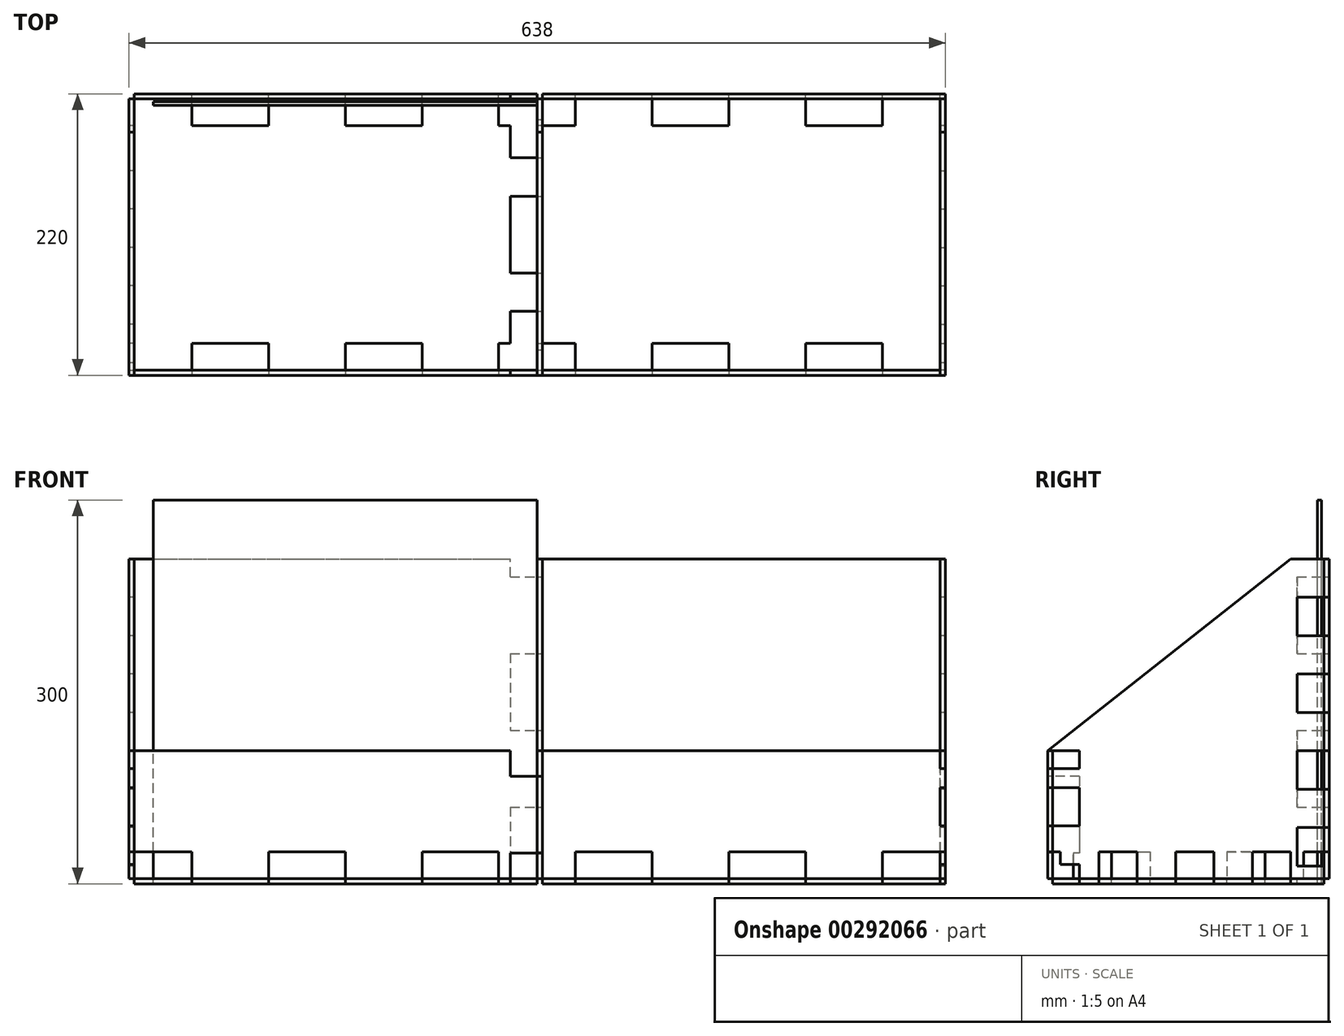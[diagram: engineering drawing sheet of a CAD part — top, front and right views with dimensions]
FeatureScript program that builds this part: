
annotation { "Feature Type Name" : "Feature", "Feature Type Description" : "" }
export const myFeature = defineFeature(function(context is Context, id is Id, definition is map)
    precondition{}
    {
        {
            var Q0;
            Q0=qCreatedBy(makeId("Top.planeOp"),FACE);
            var sketch = newSketch(context, id + "F0", { "sketchPlane" : qUnion([Q0])});
            skLineSegment(sketch, "E0.bottom", {"start": v(-319, 110) * mm, "end": v(319, 110) * mm});
            skLineSegment(sketch, "E0.top", {"start": v(-319, -110) * mm, "end": v(319, -110) * mm});
            skLineSegment(sketch, "E0.left", {"start": v(-319, 110) * mm, "end": v(-319, -110) * mm});
            skLineSegment(sketch, "E0.right", {"start": v(319, 110) * mm, "end": v(319, -110) * mm});
            skPoint(sketch, "E0.middle", {"position": v(0, 0) * mm});
            skLineSegment(sketch, "E1.bottom", {"start": v(-313, 104) * mm, "end": v(-3, 104) * mm, "construction": true});
            skLineSegment(sketch, "E1.top", {"start": v(-313, -104) * mm, "end": v(-3, -104) * mm, "construction": true});
            skLineSegment(sketch, "E1.left", {"start": v(-313, 104) * mm, "end": v(-313, -104) * mm, "construction": true});
            skLineSegment(sketch, "E1.right", {"start": v(-3, 104) * mm, "end": v(-3, -104) * mm, "construction": true});
            skPoint(sketch, "E1.middle", {"position": v(-158, 0) * mm});
            skSolve(sketch);
        }
        {
            var Q0;
            Q0 = qSketchRegion(id + "F0", true);
            extrude(context, id + "F1", {"entities" : qUnion([Q0]), "depth" : 4 * mm});
        }
        {
            var Q0;
            Q0=makeQuery(id+"F1.opExtrude","CAP_FACE",FACE,{"disambiguationData":[OSD([sQuery(id+"F0.wireOp",EDGE,"E0.bottom"),sQuery(id+"F0.wireOp",EDGE,"E0.top"),sQuery(id+"F0.wireOp",EDGE,"E0.left"),sQuery(id+"F0.wireOp",EDGE,"E0.right")])],"isStart":false});
            var sketch = newSketch(context, id + "F2", { "sketchPlane" : qUnion([Q0])});
            skLineSegment(sketch, "E2.bottom", {"start": v(-319, 110) * mm, "end": v(319, 110) * mm});
            skLineSegment(sketch, "E2.top", {"start": v(-319, 106) * mm, "end": v(319, 106) * mm});
            skLineSegment(sketch, "E2.left", {"start": v(-319, 110) * mm, "end": v(-319, 106) * mm});
            skLineSegment(sketch, "E2.right", {"start": v(319, 110) * mm, "end": v(319, 106) * mm});
            skLineSegment(sketch, "E3.bottom", {"start": v(319, -110) * mm, "end": v(-319, -110) * mm});
            skLineSegment(sketch, "E3.top", {"start": v(319, -106) * mm, "end": v(-319, -106) * mm});
            skLineSegment(sketch, "E3.left", {"start": v(319, -110) * mm, "end": v(319, -106) * mm});
            skLineSegment(sketch, "E3.right", {"start": v(-319, -110) * mm, "end": v(-319, -106) * mm});
            skSolve(sketch);
        }
        {
            var Q0;
            Q0=makeQuery(id+"F2.imprint","IMPRINT",FACE,{"disambiguationData":[TD([[makeQuery(id+"F2.imprint","IMPRINT",EDGE,{"derivedFrom":sQuery(id+"F2.wireOp",EDGE,"E3.bottom")}),1.0]])]});
            extrude(context, id + "F3", {"entities" : qUnion([Q0]), "depth" : 100 * mm, "hasSecondDirection" : true, "secondDirectionOppositeDirection" : true, "secondDirectionDepth" : 4 * mm});
        }
        {
            var Q0;
            Q0=makeQuery(id+"F1.opExtrude","CAP_FACE",FACE,{"disambiguationData":[OSD([sQuery(id+"F0.wireOp",EDGE,"E0.bottom"),sQuery(id+"F0.wireOp",EDGE,"E0.top"),sQuery(id+"F0.wireOp",EDGE,"E0.left"),sQuery(id+"F0.wireOp",EDGE,"E0.right")])],"isStart":false});
            var sketch = newSketch(context, id + "F4", { "sketchPlane" : qUnion([Q0])});
            skLineSegment(sketch, "E4.bottom", {"start": v(-319, 110) * mm, "end": v(319, 110) * mm});
            skLineSegment(sketch, "E4.top", {"start": v(-319, 106) * mm, "end": v(319, 106) * mm});
            skLineSegment(sketch, "E4.left", {"start": v(-319, 110) * mm, "end": v(-319, 106) * mm});
            skLineSegment(sketch, "E4.right", {"start": v(319, 110) * mm, "end": v(319, 106) * mm});
            skSolve(sketch);
        }
        {
            var Q0;
            Q0 = qSketchRegion(id + "F4", true);
            extrude(context, id + "F5", {"entities" : qUnion([Q0]), "depth" : 250 * mm, "hasSecondDirection" : true, "secondDirectionOppositeDirection" : true, "secondDirectionDepth" : 4 * mm});
        }
        {
            var Q0;
            Q0=makeQuery(id+"F1.opExtrude","SWEPT_FACE",FACE,{"disambiguationData":[OSD([sQuery(id+"F0.wireOp",EDGE,"E0.left")])]});
            var sketch = newSketch(context, id + "F6", { "sketchPlane" : qUnion([Q0])});
            skLineSegment(sketch, "E5", {"start": v(-110, 0) * mm, "end": v(110, 0) * mm});
            skLineSegment(sketch, "E6", {"start": v(110, 0) * mm, "end": v(110, 104) * mm});
            skLineSegment(sketch, "E7", {"start": v(110, 104) * mm, "end": v(-80, 254) * mm});
            skLineSegment(sketch, "E8", {"start": v(-80, 254) * mm, "end": v(-110, 254) * mm});
            skLineSegment(sketch, "E9", {"start": v(-110, 254) * mm, "end": v(-110, 0) * mm});
            skSolve(sketch);
        }
        {
            var Q0;
            Q0 = qSketchRegion(id + "F6", true);
            extrude(context, id + "F7", {"entities" : qUnion([Q0]), "oppositeDirection" : true, "depth" : 4 * mm});
        }
        {
            var Q0;
            Q0=qCreatedBy(makeId("Right.planeOp"),FACE);
            var Q1;
            Q1=makeQuery(id+"F7.opExtrude","CAP_FACE",FACE,{"disambiguationData":[OSD([sQuery(id+"F6.wireOp",EDGE,"E5"),sQuery(id+"F6.wireOp",EDGE,"E6"),sQuery(id+"F6.wireOp",EDGE,"E7"),sQuery(id+"F6.wireOp",EDGE,"E8"),sQuery(id+"F6.wireOp",EDGE,"E9")])],"isStart":false});
            cPlane(context, id + "F8", {"entities" : qUnion([Q0, Q1]), "cplaneType" : CPlaneType.MID_PLANE, "offset" : 0 * mm, "width" : 150 * mm, "height" : 150 * mm});
        }
        {
            var Q0;
            Q0=makeQuery(id+"F7.opExtrude","SWEPT_BODY",BODY,{"disambiguationData":[OSD([sQuery(id+"F6.wireOp",EDGE,"E5"),sQuery(id+"F6.wireOp",EDGE,"E6"),sQuery(id+"F6.wireOp",EDGE,"E7"),sQuery(id+"F6.wireOp",EDGE,"E8"),sQuery(id+"F6.wireOp",EDGE,"E9")])]});
            var Q1;
            Q1=qCreatedBy(id+"F8.planeOp",FACE);
            mirror(context, id + "F9", {"entities" : qUnion([Q0]), "mirrorPlane" : qUnion([Q1])});
        }
        {
            var Q0;
            Q0=makeQuery(id+"F9.opPattern","COPY",FACE,{"derivedFrom":makeQuery(id+"F7.opExtrude","CAP_FACE",FACE,{"disambiguationData":[OSD([sQuery(id+"F6.wireOp",EDGE,"E5"),sQuery(id+"F6.wireOp",EDGE,"E6"),sQuery(id+"F6.wireOp",EDGE,"E7"),sQuery(id+"F6.wireOp",EDGE,"E8"),sQuery(id+"F6.wireOp",EDGE,"E9")])],"isStart":false}),"instanceName":"1"});
            var sketch = newSketch(context, id + "F10", { "sketchPlane" : qUnion([Q0])});
            skLineSegment(sketch, "E10.bottom", {"start": v(-104, 0) * mm, "end": v(-101, 0) * mm});
            skLineSegment(sketch, "E10.top", {"start": v(-104, 300) * mm, "end": v(-101, 300) * mm});
            skLineSegment(sketch, "E10.left", {"start": v(-104, 0) * mm, "end": v(-104, 300) * mm});
            skLineSegment(sketch, "E10.right", {"start": v(-101, 0) * mm, "end": v(-101, 300) * mm});
            skSolve(sketch);
        }
        {
            var Q0;
            Q0 = qSketchRegion(id + "F10", true);
            extrude(context, id + "F11", {"entities" : qUnion([Q0]), "depth" : 300 * mm});
        }
        {
            var Q0;
            Q0=makeQuery(id+"F7.opExtrude","CAP_FACE",FACE,{"disambiguationData":[OSD([sQuery(id+"F6.wireOp",EDGE,"E5"),sQuery(id+"F6.wireOp",EDGE,"E6"),sQuery(id+"F6.wireOp",EDGE,"E7"),sQuery(id+"F6.wireOp",EDGE,"E8"),sQuery(id+"F6.wireOp",EDGE,"E9")])],"isStart":true});
            var sketch = newSketch(context, id + "F12", { "sketchPlane" : qUnion([Q0])});
            skLineSegment(sketch, "E11.bottom", {"start": v(-110, 254) * mm, "end": v(-106, 254) * mm});
            skLineSegment(sketch, "E11.top", {"start": v(-110, 224) * mm, "end": v(-106, 224) * mm});
            skLineSegment(sketch, "E11.left", {"start": v(-110, 254) * mm, "end": v(-110, 224) * mm});
            skLineSegment(sketch, "E11.right", {"start": v(-106, 254) * mm, "end": v(-106, 224) * mm});
            skLineSegment(sketch, "E12.bottom", {"start": v(-110, 194) * mm, "end": v(-106, 194) * mm});
            skLineSegment(sketch, "E12.top", {"start": v(-110, 164) * mm, "end": v(-106, 164) * mm});
            skLineSegment(sketch, "E12.left", {"start": v(-110, 194) * mm, "end": v(-110, 164) * mm});
            skLineSegment(sketch, "E12.right", {"start": v(-106, 194) * mm, "end": v(-106, 164) * mm});
            skLineSegment(sketch, "E13.bottom", {"start": v(-110, 134) * mm, "end": v(-106, 134) * mm});
            skLineSegment(sketch, "E13.top", {"start": v(-110, 104) * mm, "end": v(-106, 104) * mm});
            skLineSegment(sketch, "E13.left", {"start": v(-110, 134) * mm, "end": v(-110, 104) * mm});
            skLineSegment(sketch, "E13.right", {"start": v(-106, 134) * mm, "end": v(-106, 104) * mm});
            skLineSegment(sketch, "E14.bottom", {"start": v(-110, 74) * mm, "end": v(-106, 74) * mm});
            skLineSegment(sketch, "E14.top", {"start": v(-110, 44) * mm, "end": v(-106, 44) * mm});
            skLineSegment(sketch, "E14.left", {"start": v(-110, 74) * mm, "end": v(-110, 44) * mm});
            skLineSegment(sketch, "E14.right", {"start": v(-106, 74) * mm, "end": v(-106, 44) * mm});
            skLineSegment(sketch, "E15.top", {"start": v(-110, 14) * mm, "end": v(-106, 14) * mm});
            skLineSegment(sketch, "E15.left", {"start": v(-110, 0) * mm, "end": v(-110, 14) * mm});
            skLineSegment(sketch, "E15.right", {"start": v(-106, 4) * mm, "end": v(-106, 14) * mm});
            skLineSegment(sketch, "E16.top", {"start": v(-106, 4) * mm, "end": v(-80, 4) * mm});
            skLineSegment(sketch, "E16.right", {"start": v(-80, 0) * mm, "end": v(-80, 4) * mm});
            skLineSegment(sketch, "E17", {"start": v(-110, 0) * mm, "end": v(-80, 0) * mm});
            skLineSegment(sketch, "E18.bottom", {"start": v(-50, 0) * mm, "end": v(-20, 0) * mm});
            skLineSegment(sketch, "E18.top", {"start": v(-50, 4) * mm, "end": v(-20, 4) * mm});
            skLineSegment(sketch, "E18.left", {"start": v(-50, 0) * mm, "end": v(-50, 4) * mm});
            skLineSegment(sketch, "E18.right", {"start": v(-20, 0) * mm, "end": v(-20, 4) * mm});
            skLineSegment(sketch, "E19.bottom", {"start": v(10, 0) * mm, "end": v(40, 0) * mm});
            skLineSegment(sketch, "E19.top", {"start": v(10, 4) * mm, "end": v(40, 4) * mm});
            skLineSegment(sketch, "E19.left", {"start": v(10, 0) * mm, "end": v(10, 4) * mm});
            skLineSegment(sketch, "E19.right", {"start": v(40, 0) * mm, "end": v(40, 4) * mm});
            skLineSegment(sketch, "E20.bottom", {"start": v(70, 0) * mm, "end": v(100, 0) * mm});
            skLineSegment(sketch, "E20.top", {"start": v(70, 4) * mm, "end": v(100, 4) * mm});
            skLineSegment(sketch, "E20.left", {"start": v(70, 0) * mm, "end": v(70, 4) * mm});
            skLineSegment(sketch, "E20.right", {"start": v(100, 0) * mm, "end": v(100, 4) * mm});
            skLineSegment(sketch, "E21.bottom", {"start": v(110, 15.15) * mm, "end": v(106, 15.15) * mm});
            skLineSegment(sketch, "E21.top", {"start": v(110, 45.15) * mm, "end": v(106, 45.15) * mm});
            skLineSegment(sketch, "E21.left", {"start": v(110, 15.15) * mm, "end": v(110, 45.15) * mm});
            skLineSegment(sketch, "E21.right", {"start": v(106, 15.15) * mm, "end": v(106, 45.15) * mm});
            skLineSegment(sketch, "E22.left", {"start": v(110, 75.15) * mm, "end": v(110, 90.15) * mm});
            skLineSegment(sketch, "E22.right", {"start": v(106, 75.15) * mm, "end": v(106, 90.15) * mm});
            skLineSegment(sketch, "E23", {"start": v(106, 75.15) * mm, "end": v(110, 75.15) * mm});
            skLineSegment(sketch, "E24", {"start": v(106, 90.15) * mm, "end": v(110, 90.15) * mm});
            skSolve(sketch);
        }
        {
            var Q0;
            Q0 = qSketchRegion(id + "F12", true);
            extrude(context, id + "F13", {"entities" : qUnion([Q0]), "operationType" : NewBodyOperationType.REMOVE, "oppositeDirection" : true, "depth" : 4 * mm});
        }
        {
            var Q0;
            Q0=makeQuery(id+"F7.opExtrude","SWEPT_BODY",BODY,{"disambiguationData":[OSD([sQuery(id+"F6.wireOp",EDGE,"E5"),sQuery(id+"F6.wireOp",EDGE,"E6"),sQuery(id+"F6.wireOp",EDGE,"E7"),sQuery(id+"F6.wireOp",EDGE,"E8"),sQuery(id+"F6.wireOp",EDGE,"E9")])]});
            var Q1;
            Q1=qCreatedBy(makeId("Right.planeOp"),FACE);
            mirror(context, id + "F14", {"entities" : qUnion([Q0]), "mirrorPlane" : qUnion([Q1])});
        }
        {
            var Q0;
            Q0=makeQuery(id+"F3.opExtrude","SWEPT_FACE",FACE,{"disambiguationData":[OSD([sQuery(id+"F2.wireOp",EDGE,"E3.bottom")])]});
            var sketch = newSketch(context, id + "F15", { "sketchPlane" : qUnion([Q0])});
            skLineSegment(sketch, "E25.bottom", {"start": v(-319, 104) * mm, "end": v(-315, 104) * mm});
            skLineSegment(sketch, "E25.top", {"start": v(-319, 90.15) * mm, "end": v(-315, 90.15) * mm});
            skLineSegment(sketch, "E25.left", {"start": v(-319, 104) * mm, "end": v(-319, 90.15) * mm});
            skLineSegment(sketch, "E25.right", {"start": v(-315, 104) * mm, "end": v(-315, 90.15) * mm});
            skLineSegment(sketch, "E26.bottom", {"start": v(-319, 45.15) * mm, "end": v(-315, 45.15) * mm});
            skLineSegment(sketch, "E26.top", {"start": v(-319, 75.15) * mm, "end": v(-315, 75.15) * mm});
            skLineSegment(sketch, "E26.left", {"start": v(-319, 45.15) * mm, "end": v(-319, 75.15) * mm});
            skLineSegment(sketch, "E26.right", {"start": v(-315, 45.15) * mm, "end": v(-315, 75.15) * mm});
            skLineSegment(sketch, "E27.top", {"start": v(-319, 15.15) * mm, "end": v(-315, 15.15) * mm});
            skLineSegment(sketch, "E27.left", {"start": v(-319, 0) * mm, "end": v(-319, 15.15) * mm});
            skLineSegment(sketch, "E28.MirrorCS", {"start": v(319, 104) * mm, "end": v(315, 104) * mm});
            skLineSegment(sketch, "E29.MirrorCS", {"start": v(319, 90.15) * mm, "end": v(315, 90.15) * mm});
            skLineSegment(sketch, "E30.MirrorCS", {"start": v(319, 75.15) * mm, "end": v(315, 75.15) * mm});
            skLineSegment(sketch, "E31.MirrorCS", {"start": v(319, 0) * mm, "end": v(315, 0) * mm});
            skLineSegment(sketch, "E32.MirrorCS", {"start": v(319, 15.15) * mm, "end": v(315, 15.15) * mm});
            skLineSegment(sketch, "E33.MirrorCS", {"start": v(319, 45.15) * mm, "end": v(315, 45.15) * mm});
            skLineSegment(sketch, "E34.MirrorCS", {"start": v(315, 0) * mm, "end": v(315, 15.15) * mm});
            skLineSegment(sketch, "E35.MirrorCS", {"start": v(319, 0) * mm, "end": v(319, 15.15) * mm});
            skLineSegment(sketch, "E36.MirrorCS", {"start": v(319, 104) * mm, "end": v(319, 90.15) * mm});
            skLineSegment(sketch, "E37.MirrorCS", {"start": v(315, 104) * mm, "end": v(315, 90.15) * mm});
            skLineSegment(sketch, "E38.MirrorCS", {"start": v(315, 45.15) * mm, "end": v(315, 75.15) * mm});
            skLineSegment(sketch, "E39.MirrorCS", {"start": v(319, 45.15) * mm, "end": v(319, 75.15) * mm});
            skLineSegment(sketch, "E40.bottom", {"start": v(-270, 0) * mm, "end": v(-210, 0) * mm});
            skLineSegment(sketch, "E40.top", {"start": v(-270, 4) * mm, "end": v(-210, 4) * mm});
            skLineSegment(sketch, "E40.left", {"start": v(-270, 0) * mm, "end": v(-270, 4) * mm});
            skLineSegment(sketch, "E40.right", {"start": v(-210, 0) * mm, "end": v(-210, 4) * mm});
            skLineSegment(sketch, "E41.bottom", {"start": v(-150, 0) * mm, "end": v(-90, 0) * mm});
            skLineSegment(sketch, "E41.top", {"start": v(-150, 4) * mm, "end": v(-90, 4) * mm});
            skLineSegment(sketch, "E41.left", {"start": v(-150, 0) * mm, "end": v(-150, 4) * mm});
            skLineSegment(sketch, "E41.right", {"start": v(-90, 0) * mm, "end": v(-90, 4) * mm});
            skLineSegment(sketch, "E42.bottom", {"start": v(-30, 0) * mm, "end": v(30, 0) * mm});
            skLineSegment(sketch, "E42.top", {"start": v(-30, 4) * mm, "end": v(30, 4) * mm});
            skLineSegment(sketch, "E42.left", {"start": v(-30, 0) * mm, "end": v(-30, 4) * mm});
            skLineSegment(sketch, "E42.right", {"start": v(30, 0) * mm, "end": v(30, 4) * mm});
            skPoint(sketch, "E43.oppositeSnap0", {"position": v(0, 4) * mm});
            skLineSegment(sketch, "E43.bottom", {"start": v(90, 0) * mm, "end": v(150, 0) * mm});
            skLineSegment(sketch, "E43.top", {"start": v(90, 4) * mm, "end": v(150, 4) * mm});
            skLineSegment(sketch, "E43.left", {"start": v(90, 0) * mm, "end": v(90, 4) * mm});
            skLineSegment(sketch, "E43.right", {"start": v(150, 0) * mm, "end": v(150, 4) * mm});
            skLineSegment(sketch, "E44.bottom", {"start": v(210, 0) * mm, "end": v(270, 0) * mm});
            skLineSegment(sketch, "E44.top", {"start": v(210, 4) * mm, "end": v(270, 4) * mm});
            skLineSegment(sketch, "E44.left", {"start": v(210, 0) * mm, "end": v(210, 4) * mm});
            skLineSegment(sketch, "E44.right", {"start": v(270, 0) * mm, "end": v(270, 4) * mm});
            skLineSegment(sketch, "E45", {"start": v(-319, 0) * mm, "end": v(-315, 0) * mm});
            skLineSegment(sketch, "E46", {"start": v(-315, 0) * mm, "end": v(-315, 15.15) * mm});
            skLineSegment(sketch, "E47.bottom", {"start": v(0, 84) * mm, "end": v(4.3, 84) * mm});
            skLineSegment(sketch, "E47.top", {"start": v(0, 24) * mm, "end": v(4.3, 24) * mm});
            skLineSegment(sketch, "E47.left", {"start": v(0, 84) * mm, "end": v(0, 24) * mm});
            skLineSegment(sketch, "E47.right", {"start": v(4.3, 84) * mm, "end": v(4.3, 24) * mm});
            skSolve(sketch);
        }
        {
            var Q0;
            Q0 = qSketchRegion(id + "F15", true);
            extrude(context, id + "F16", {"entities" : qUnion([Q0]), "operationType" : NewBodyOperationType.REMOVE, "oppositeDirection" : true, "depth" : 25 * mm});
        }
        {
            var Q0;
            Q0=makeQuery(id+"F9.opPattern","COPY",FACE,{"derivedFrom":makeQuery(id+"F7.opExtrude","CAP_FACE",FACE,{"disambiguationData":[OSD([sQuery(id+"F6.wireOp",EDGE,"E5"),sQuery(id+"F6.wireOp",EDGE,"E6"),sQuery(id+"F6.wireOp",EDGE,"E7"),sQuery(id+"F6.wireOp",EDGE,"E8"),sQuery(id+"F6.wireOp",EDGE,"E9")])],"isStart":true}),"instanceName":"1"});
            var sketch = newSketch(context, id + "F17", { "sketchPlane" : qUnion([Q0])});
            skLineSegment(sketch, "E48.bottom", {"start": v(-110, 84) * mm, "end": v(-106, 84) * mm});
            skLineSegment(sketch, "E48.top", {"start": v(-110, 104) * mm, "end": v(-106, 104) * mm});
            skLineSegment(sketch, "E48.left", {"start": v(-110, 84) * mm, "end": v(-110, 104) * mm});
            skLineSegment(sketch, "E48.right", {"start": v(-106, 84) * mm, "end": v(-106, 104) * mm});
            skLineSegment(sketch, "E49.bottom", {"start": v(-110, 24) * mm, "end": v(-106, 24) * mm});
            skLineSegment(sketch, "E49.top", {"start": v(-110, -7.27) * mm, "end": v(-106, -7.27) * mm});
            skLineSegment(sketch, "E49.left", {"start": v(-110, 24) * mm, "end": v(-110, -7.27) * mm});
            skLineSegment(sketch, "E49.right", {"start": v(-106, 24) * mm, "end": v(-106, -7.27) * mm});
            skLineSegment(sketch, "E50.bottom", {"start": v(-30, 0) * mm, "end": v(30, 0) * mm});
            skLineSegment(sketch, "E50.top", {"start": v(-30, 4) * mm, "end": v(30, 4) * mm});
            skLineSegment(sketch, "E50.left", {"start": v(-30, 0) * mm, "end": v(-30, 4) * mm});
            skLineSegment(sketch, "E50.right", {"start": v(30, 0) * mm, "end": v(30, 4) * mm});
            skLineSegment(sketch, "E51.bottom", {"start": v(-60, 0) * mm, "end": v(-90, 0) * mm});
            skLineSegment(sketch, "E51.top", {"start": v(-60, 4) * mm, "end": v(-90, 4) * mm});
            skLineSegment(sketch, "E51.left", {"start": v(-60, 0) * mm, "end": v(-60, 4) * mm});
            skLineSegment(sketch, "E51.right", {"start": v(-90, 0) * mm, "end": v(-90, 4) * mm});
            skLineSegment(sketch, "E52.bottom", {"start": v(60, 0) * mm, "end": v(90, 0) * mm});
            skLineSegment(sketch, "E52.top", {"start": v(60, 4) * mm, "end": v(90, 4) * mm});
            skLineSegment(sketch, "E52.left", {"start": v(60, 0) * mm, "end": v(60, 4) * mm});
            skLineSegment(sketch, "E52.right", {"start": v(90, 0) * mm, "end": v(90, 4) * mm});
            skLineSegment(sketch, "E53.bottom", {"start": v(110, 0) * mm, "end": v(106, 0) * mm});
            skLineSegment(sketch, "E53.top", {"start": v(110, 60) * mm, "end": v(106, 60) * mm});
            skLineSegment(sketch, "E53.left", {"start": v(110, 0) * mm, "end": v(110, 60) * mm});
            skLineSegment(sketch, "E53.right", {"start": v(106, 0) * mm, "end": v(106, 60) * mm});
            skLineSegment(sketch, "E54.bottom", {"start": v(110, 120) * mm, "end": v(106, 120) * mm});
            skLineSegment(sketch, "E54.top", {"start": v(110, 180) * mm, "end": v(106, 180) * mm});
            skLineSegment(sketch, "E54.left", {"start": v(110, 120) * mm, "end": v(110, 180) * mm});
            skLineSegment(sketch, "E54.right", {"start": v(106, 120) * mm, "end": v(106, 180) * mm});
            skLineSegment(sketch, "E55.bottom", {"start": v(110, 240) * mm, "end": v(106, 240) * mm});
            skLineSegment(sketch, "E55.top", {"start": v(110, 300) * mm, "end": v(106, 300) * mm});
            skLineSegment(sketch, "E55.left", {"start": v(110, 240) * mm, "end": v(110, 300) * mm});
            skLineSegment(sketch, "E55.right", {"start": v(106, 240) * mm, "end": v(106, 300) * mm});
            skSolve(sketch);
        }
        {
            var Q0;
            Q0 = qSketchRegion(id + "F17", true);
            extrude(context, id + "F18", {"entities" : qUnion([Q0]), "operationType" : NewBodyOperationType.REMOVE, "oppositeDirection" : true, "depth" : 25 * mm});
        }
        {
            var Q0;
            Q0=makeQuery(id+"F5.opExtrude","SWEPT_FACE",FACE,{"disambiguationData":[OSD([sQuery(id+"F4.wireOp",EDGE,"E4.bottom")])]});
            var sketch = newSketch(context, id + "F19", { "sketchPlane" : qUnion([Q0])});
            skLineSegment(sketch, "E56.bottom", {"start": v(-4.3, 240) * mm, "end": v(0, 240) * mm});
            skLineSegment(sketch, "E56.top", {"start": v(-4.3, 180) * mm, "end": v(0, 180) * mm});
            skLineSegment(sketch, "E56.left", {"start": v(-4.3, 240) * mm, "end": v(-4.3, 180) * mm});
            skLineSegment(sketch, "E56.right", {"start": v(0, 240) * mm, "end": v(0, 180) * mm});
            skLineSegment(sketch, "E57.bottom", {"start": v(0, 120) * mm, "end": v(-4.3, 120) * mm});
            skLineSegment(sketch, "E57.top", {"start": v(0, 60) * mm, "end": v(-4.3, 60) * mm});
            skLineSegment(sketch, "E57.left", {"start": v(0, 120) * mm, "end": v(0, 60) * mm});
            skLineSegment(sketch, "E57.right", {"start": v(-4.3, 120) * mm, "end": v(-4.3, 60) * mm});
            skLineSegment(sketch, "E58.bottom", {"start": v(319, 224) * mm, "end": v(315, 224) * mm});
            skLineSegment(sketch, "E58.top", {"start": v(319, 194) * mm, "end": v(315, 194) * mm});
            skLineSegment(sketch, "E58.left", {"start": v(319, 224) * mm, "end": v(319, 194) * mm});
            skLineSegment(sketch, "E58.right", {"start": v(315, 224) * mm, "end": v(315, 194) * mm});
            skLineSegment(sketch, "E59.bottom", {"start": v(319, 164) * mm, "end": v(315, 164) * mm});
            skLineSegment(sketch, "E59.top", {"start": v(319, 134) * mm, "end": v(315, 134) * mm});
            skLineSegment(sketch, "E59.left", {"start": v(319, 164) * mm, "end": v(319, 134) * mm});
            skLineSegment(sketch, "E59.right", {"start": v(315, 164) * mm, "end": v(315, 134) * mm});
            skLineSegment(sketch, "E60.bottom", {"start": v(319, 104) * mm, "end": v(315, 104) * mm});
            skLineSegment(sketch, "E60.top", {"start": v(319, 74) * mm, "end": v(315, 74) * mm});
            skLineSegment(sketch, "E60.left", {"start": v(319, 104) * mm, "end": v(319, 74) * mm});
            skLineSegment(sketch, "E60.right", {"start": v(315, 104) * mm, "end": v(315, 74) * mm});
            skLineSegment(sketch, "E61.bottom", {"start": v(319, 44) * mm, "end": v(315, 44) * mm});
            skLineSegment(sketch, "E61.top", {"start": v(319, 14) * mm, "end": v(315, 14) * mm});
            skLineSegment(sketch, "E61.left", {"start": v(319, 44) * mm, "end": v(319, 14) * mm});
            skLineSegment(sketch, "E61.right", {"start": v(315, 44) * mm, "end": v(315, 14) * mm});
            skLineSegment(sketch, "E62.MirrorCS", {"start": v(-319, 224) * mm, "end": v(-315, 224) * mm});
            skLineSegment(sketch, "E63.MirrorCS", {"start": v(-319, 104) * mm, "end": v(-315, 104) * mm});
            skLineSegment(sketch, "E64.MirrorCS", {"start": v(-319, 44) * mm, "end": v(-315, 44) * mm});
            skLineSegment(sketch, "E65.MirrorCS", {"start": v(-319, 164) * mm, "end": v(-315, 164) * mm});
            skLineSegment(sketch, "E66.MirrorCS", {"start": v(-319, 74) * mm, "end": v(-315, 74) * mm});
            skLineSegment(sketch, "E67.MirrorCS", {"start": v(-319, 14) * mm, "end": v(-315, 14) * mm});
            skLineSegment(sketch, "E68.MirrorCS", {"start": v(-319, 194) * mm, "end": v(-315, 194) * mm});
            skLineSegment(sketch, "E69.MirrorCS", {"start": v(-319, 134) * mm, "end": v(-315, 134) * mm});
            skLineSegment(sketch, "E70.MirrorCS", {"start": v(-315, 164) * mm, "end": v(-315, 134) * mm});
            skLineSegment(sketch, "E71.MirrorCS", {"start": v(-315, 104) * mm, "end": v(-315, 74) * mm});
            skLineSegment(sketch, "E72.MirrorCS", {"start": v(-315, 224) * mm, "end": v(-315, 194) * mm});
            skLineSegment(sketch, "E73.MirrorCS", {"start": v(-319, 104) * mm, "end": v(-319, 74) * mm});
            skLineSegment(sketch, "E74.MirrorCS", {"start": v(-315, 44) * mm, "end": v(-315, 14) * mm});
            skLineSegment(sketch, "E75.MirrorCS", {"start": v(-319, 44) * mm, "end": v(-319, 14) * mm});
            skLineSegment(sketch, "E76.MirrorCS", {"start": v(-319, 224) * mm, "end": v(-319, 194) * mm});
            skLineSegment(sketch, "E77.MirrorCS", {"start": v(-319, 164) * mm, "end": v(-319, 134) * mm});
            skLineSegment(sketch, "E78.bottom", {"start": v(-30, 0) * mm, "end": v(30, 0) * mm});
            skLineSegment(sketch, "E78.top", {"start": v(-30, 4) * mm, "end": v(30, 4) * mm});
            skLineSegment(sketch, "E78.left", {"start": v(-30, 0) * mm, "end": v(-30, 4) * mm});
            skLineSegment(sketch, "E78.right", {"start": v(30, 0) * mm, "end": v(30, 4) * mm});
            skLineSegment(sketch, "E79.bottom", {"start": v(-90, 0) * mm, "end": v(-150, 0) * mm});
            skLineSegment(sketch, "E79.top", {"start": v(-90, 4) * mm, "end": v(-150, 4) * mm});
            skLineSegment(sketch, "E79.left", {"start": v(-90, 0) * mm, "end": v(-90, 4) * mm});
            skLineSegment(sketch, "E79.right", {"start": v(-150, 0) * mm, "end": v(-150, 4) * mm});
            skLineSegment(sketch, "E80.bottom", {"start": v(-210, 0) * mm, "end": v(-270, 0) * mm});
            skLineSegment(sketch, "E80.top", {"start": v(-210, 4) * mm, "end": v(-270, 4) * mm});
            skLineSegment(sketch, "E80.left", {"start": v(-210, 0) * mm, "end": v(-210, 4) * mm});
            skLineSegment(sketch, "E80.right", {"start": v(-270, 0) * mm, "end": v(-270, 4) * mm});
            skLineSegment(sketch, "E81.MirrorCS", {"start": v(270, 0) * mm, "end": v(270, 4) * mm});
            skLineSegment(sketch, "E82.MirrorCS", {"start": v(210, 0) * mm, "end": v(210, 4) * mm});
            skLineSegment(sketch, "E83.MirrorCS", {"start": v(150, 0) * mm, "end": v(150, 4) * mm});
            skLineSegment(sketch, "E84.MirrorCS", {"start": v(90, 0) * mm, "end": v(90, 4) * mm});
            skLineSegment(sketch, "E85.MirrorCS", {"start": v(210, 4) * mm, "end": v(270, 4) * mm});
            skLineSegment(sketch, "E86.MirrorCS", {"start": v(90, 0) * mm, "end": v(150, 0) * mm});
            skLineSegment(sketch, "E87.MirrorCS", {"start": v(90, 4) * mm, "end": v(150, 4) * mm});
            skLineSegment(sketch, "E88.MirrorCS", {"start": v(210, 0) * mm, "end": v(270, 0) * mm});
            skSolve(sketch);
        }
        {
            var Q0;
            Q0 = qSketchRegion(id + "F19", true);
            extrude(context, id + "F20", {"entities" : qUnion([Q0]), "operationType" : NewBodyOperationType.REMOVE, "oppositeDirection" : true, "depth" : 25 * mm});
        }
        {
            var Q0;
            Q0=makeQuery(id+"F1.opExtrude","CAP_FACE",FACE,{"disambiguationData":[OSD([sQuery(id+"F0.wireOp",EDGE,"E0.bottom"),sQuery(id+"F0.wireOp",EDGE,"E0.top"),sQuery(id+"F0.wireOp",EDGE,"E0.left"),sQuery(id+"F0.wireOp",EDGE,"E0.right")])],"isStart":true});
            var sketch = newSketch(context, id + "F21", { "sketchPlane" : qUnion([Q0])});
            skLineSegment(sketch, "E89.bottom", {"start": v(0, 60) * mm, "end": v(4.3, 60) * mm});
            skLineSegment(sketch, "E89.top", {"start": v(0, 30) * mm, "end": v(4.3, 30) * mm});
            skLineSegment(sketch, "E89.left", {"start": v(0, 60) * mm, "end": v(0, 30) * mm});
            skLineSegment(sketch, "E89.right", {"start": v(4.3, 60) * mm, "end": v(4.3, 30) * mm});
            skLineSegment(sketch, "E90.bottom", {"start": v(30, 110) * mm, "end": v(90, 110) * mm});
            skLineSegment(sketch, "E90.top", {"start": v(30, 106) * mm, "end": v(90, 106) * mm});
            skLineSegment(sketch, "E90.left", {"start": v(30, 110) * mm, "end": v(30, 106) * mm});
            skLineSegment(sketch, "E90.right", {"start": v(90, 110) * mm, "end": v(90, 106) * mm});
            skLineSegment(sketch, "E91.bottom", {"start": v(150, 110) * mm, "end": v(210, 110) * mm});
            skLineSegment(sketch, "E91.top", {"start": v(150, 106) * mm, "end": v(210, 106) * mm});
            skLineSegment(sketch, "E91.left", {"start": v(150, 110) * mm, "end": v(150, 106) * mm});
            skLineSegment(sketch, "E91.right", {"start": v(210, 110) * mm, "end": v(210, 106) * mm});
            skLineSegment(sketch, "E92.bottom", {"start": v(270, 110) * mm, "end": v(319, 110) * mm});
            skLineSegment(sketch, "E92.top", {"start": v(270, 106) * mm, "end": v(315, 106) * mm});
            skLineSegment(sketch, "E92.left", {"start": v(270, 110) * mm, "end": v(270, 106) * mm});
            skLineSegment(sketch, "E93.bottom", {"start": v(0, 90) * mm, "end": v(4.3, 90) * mm});
            skLineSegment(sketch, "E93.top", {"start": v(0, 106) * mm, "end": v(4.3, 106) * mm});
            skLineSegment(sketch, "E93.left", {"start": v(0, 90) * mm, "end": v(0, 106) * mm});
            skLineSegment(sketch, "E93.right", {"start": v(4.3, 90) * mm, "end": v(4.3, 106) * mm});
            skLineSegment(sketch, "E94.left", {"start": v(319, 106) * mm, "end": v(319, 110) * mm});
            skLineSegment(sketch, "E95.bottom", {"start": v(319, 70) * mm, "end": v(315, 70) * mm});
            skLineSegment(sketch, "E95.top", {"start": v(319, 40) * mm, "end": v(315, 40) * mm});
            skLineSegment(sketch, "E95.left", {"start": v(319, 70) * mm, "end": v(319, 40) * mm});
            skLineSegment(sketch, "E95.right", {"start": v(315, 70) * mm, "end": v(315, 40) * mm});
            skLineSegment(sketch, "E96.bottom", {"start": v(319, 10) * mm, "end": v(315, 10) * mm});
            skLineSegment(sketch, "E96.top", {"start": v(319, -20) * mm, "end": v(315, -20) * mm});
            skLineSegment(sketch, "E96.left", {"start": v(319, 10) * mm, "end": v(319, -20) * mm});
            skLineSegment(sketch, "E96.right", {"start": v(315, 10) * mm, "end": v(315, -20) * mm});
            skLineSegment(sketch, "E97.MirrorCS", {"start": v(319, -106) * mm, "end": v(319, -110) * mm});
            skLineSegment(sketch, "E98.MirrorCS", {"start": v(0, -60) * mm, "end": v(4.3, -60) * mm});
            skLineSegment(sketch, "E99.MirrorCS", {"start": v(0, -106) * mm, "end": v(4.3, -106) * mm});
            skLineSegment(sketch, "E100.MirrorCS", {"start": v(270, -110) * mm, "end": v(270, -106) * mm});
            skLineSegment(sketch, "E101.MirrorCS", {"start": v(0, -90) * mm, "end": v(0, -106) * mm});
            skLineSegment(sketch, "E102.MirrorCS", {"start": v(0, -30) * mm, "end": v(4.3, -30) * mm});
            skLineSegment(sketch, "E103.MirrorCS", {"start": v(90, -110) * mm, "end": v(90, -106) * mm});
            skLineSegment(sketch, "E104.MirrorCS", {"start": v(30, -110) * mm, "end": v(30, -106) * mm});
            skLineSegment(sketch, "E105.MirrorCS", {"start": v(0, -90) * mm, "end": v(4.3, -90) * mm});
            skLineSegment(sketch, "E106.MirrorCS", {"start": v(4.3, -90) * mm, "end": v(4.3, -106) * mm});
            skLineSegment(sketch, "E107.MirrorCS", {"start": v(150, -110) * mm, "end": v(150, -106) * mm});
            skLineSegment(sketch, "E108.MirrorCS", {"start": v(210, -110) * mm, "end": v(210, -106) * mm});
            skLineSegment(sketch, "E109.MirrorCS", {"start": v(4.3, -60) * mm, "end": v(4.3, -30) * mm});
            skLineSegment(sketch, "E110.MirrorCS", {"start": v(270, -106) * mm, "end": v(315, -106) * mm});
            skLineSegment(sketch, "E111.MirrorCS", {"start": v(30, -106) * mm, "end": v(90, -106) * mm});
            skLineSegment(sketch, "E112.MirrorCS", {"start": v(30, -110) * mm, "end": v(90, -110) * mm});
            skLineSegment(sketch, "E113.MirrorCS", {"start": v(150, -110) * mm, "end": v(210, -110) * mm});
            skLineSegment(sketch, "E114.MirrorCS", {"start": v(0, -60) * mm, "end": v(0, -30) * mm});
            skLineSegment(sketch, "E115.MirrorCS", {"start": v(150, -106) * mm, "end": v(210, -106) * mm});
            skLineSegment(sketch, "E116.MirrorCS", {"start": v(270, -110) * mm, "end": v(319, -110) * mm});
            skLineSegment(sketch, "E117.bottom", {"start": v(319, -50) * mm, "end": v(315, -50) * mm});
            skLineSegment(sketch, "E117.top", {"start": v(319, -80) * mm, "end": v(315, -80) * mm});
            skLineSegment(sketch, "E117.left", {"start": v(319, -50) * mm, "end": v(319, -80) * mm});
            skLineSegment(sketch, "E117.right", {"start": v(315, -50) * mm, "end": v(315, -80) * mm});
            skLineSegment(sketch, "E118.MirrorCS", {"start": v(-150, 110) * mm, "end": v(-150, 106) * mm});
            skLineSegment(sketch, "E119.MirrorCS", {"start": v(-319, -50) * mm, "end": v(-315, -50) * mm});
            skLineSegment(sketch, "E120.MirrorCS", {"start": v(-319, 106) * mm, "end": v(-319, 110) * mm});
            skLineSegment(sketch, "E121.MirrorCS", {"start": v(-90, 110) * mm, "end": v(-90, 106) * mm});
            skLineSegment(sketch, "E122.MirrorCS", {"start": v(-150, -110) * mm, "end": v(-150, -106) * mm});
            skLineSegment(sketch, "E123.MirrorCS", {"start": v(-30, 110) * mm, "end": v(-30, 106) * mm});
            skLineSegment(sketch, "E124.MirrorCS", {"start": v(-319, 10) * mm, "end": v(-315, 10) * mm});
            skLineSegment(sketch, "E125.MirrorCS", {"start": v(-210, 110) * mm, "end": v(-210, 106) * mm});
            skLineSegment(sketch, "E126.MirrorCS", {"start": v(-319, 40) * mm, "end": v(-315, 40) * mm});
            skLineSegment(sketch, "E127.MirrorCS", {"start": v(-30, -110) * mm, "end": v(-30, -106) * mm});
            skLineSegment(sketch, "E128.MirrorCS", {"start": v(-319, -80) * mm, "end": v(-315, -80) * mm});
            skLineSegment(sketch, "E129.MirrorCS", {"start": v(-270, 110) * mm, "end": v(-270, 106) * mm});
            skLineSegment(sketch, "E130.MirrorCS", {"start": v(-270, -110) * mm, "end": v(-270, -106) * mm});
            skLineSegment(sketch, "E131.MirrorCS", {"start": v(-90, -110) * mm, "end": v(-90, -106) * mm});
            skLineSegment(sketch, "E132.MirrorCS", {"start": v(-319, 70) * mm, "end": v(-315, 70) * mm});
            skLineSegment(sketch, "E133.MirrorCS", {"start": v(-319, -20) * mm, "end": v(-315, -20) * mm});
            skLineSegment(sketch, "E134.MirrorCS", {"start": v(-210, -110) * mm, "end": v(-210, -106) * mm});
            skLineSegment(sketch, "E135.MirrorCS", {"start": v(-319, -106) * mm, "end": v(-319, -110) * mm});
            skLineSegment(sketch, "E136.MirrorCS", {"start": v(-315, 10) * mm, "end": v(-315, -20) * mm});
            skLineSegment(sketch, "E137.MirrorCS", {"start": v(-315, -50) * mm, "end": v(-315, -80) * mm});
            skLineSegment(sketch, "E138.MirrorCS", {"start": v(-270, -110) * mm, "end": v(-319, -110) * mm});
            skLineSegment(sketch, "E139.MirrorCS", {"start": v(-30, 106) * mm, "end": v(-90, 106) * mm});
            skLineSegment(sketch, "E140.MirrorCS", {"start": v(-30, 110) * mm, "end": v(-90, 110) * mm});
            skLineSegment(sketch, "E141.MirrorCS", {"start": v(-150, 110) * mm, "end": v(-210, 110) * mm});
            skLineSegment(sketch, "E142.MirrorCS", {"start": v(-150, 106) * mm, "end": v(-210, 106) * mm});
            skLineSegment(sketch, "E143.MirrorCS", {"start": v(-270, 110) * mm, "end": v(-319, 110) * mm});
            skLineSegment(sketch, "E144.MirrorCS", {"start": v(-150, -110) * mm, "end": v(-210, -110) * mm});
            skLineSegment(sketch, "E145.MirrorCS", {"start": v(-319, 10) * mm, "end": v(-319, -20) * mm});
            skLineSegment(sketch, "E146.MirrorCS", {"start": v(-319, 70) * mm, "end": v(-319, 40) * mm});
            skLineSegment(sketch, "E147.MirrorCS", {"start": v(-270, -106) * mm, "end": v(-315, -106) * mm});
            skLineSegment(sketch, "E148.MirrorCS", {"start": v(-270, 106) * mm, "end": v(-315, 106) * mm});
            skLineSegment(sketch, "E149.MirrorCS", {"start": v(-150, -106) * mm, "end": v(-210, -106) * mm});
            skLineSegment(sketch, "E150.MirrorCS", {"start": v(-319, -50) * mm, "end": v(-319, -80) * mm});
            skLineSegment(sketch, "E151.MirrorCS", {"start": v(-30, -110) * mm, "end": v(-90, -110) * mm});
            skLineSegment(sketch, "E152.MirrorCS", {"start": v(-315, 70) * mm, "end": v(-315, 40) * mm});
            skLineSegment(sketch, "E153.MirrorCS", {"start": v(-30, -106) * mm, "end": v(-90, -106) * mm});
            skLineSegment(sketch, "E154", {"start": v(315, -106) * mm, "end": v(319, -106) * mm});
            skPoint(sketch, "E155.orphan", {"position": v(319, -100) * mm});
            skPoint(sketch, "E94.bottom.start.orphan", {"position": v(319, 100) * mm});
            skPoint(sketch, "E94.right.start.orphan", {"position": v(315, 100) * mm});
            skPoint(sketch, "E156.MirrorCS.start.orphan", {"position": v(-319, 100) * mm});
            skPoint(sketch, "E157.MirrorCS.start.orphan", {"position": v(-315, 100) * mm});
            skLineSegment(sketch, "E158", {"start": v(-315, -106) * mm, "end": v(-319, -106) * mm});
            skPoint(sketch, "E159.orphan", {"position": v(-319, -100) * mm});
            skLineSegment(sketch, "E160", {"start": v(315, 106) * mm, "end": v(315, 100) * mm});
            skLineSegment(sketch, "E161", {"start": v(319, 100) * mm, "end": v(315, 100) * mm});
            skLineSegment(sketch, "E162", {"start": v(319, 100) * mm, "end": v(319, 106) * mm});
            skLineSegment(sketch, "E163", {"start": v(-319, 106) * mm, "end": v(-319, 100) * mm});
            skLineSegment(sketch, "E164", {"start": v(-315, 100) * mm, "end": v(-319, 100) * mm});
            skLineSegment(sketch, "E165", {"start": v(-315, 100) * mm, "end": v(-315, 106) * mm});
            skSolve(sketch);
        }
        {
            var Q0;
            Q0 = qSketchRegion(id + "F21", true);
            extrude(context, id + "F22", {"entities" : qUnion([Q0]), "operationType" : NewBodyOperationType.REMOVE, "oppositeDirection" : true, "depth" : 25 * mm});
        }
    });
